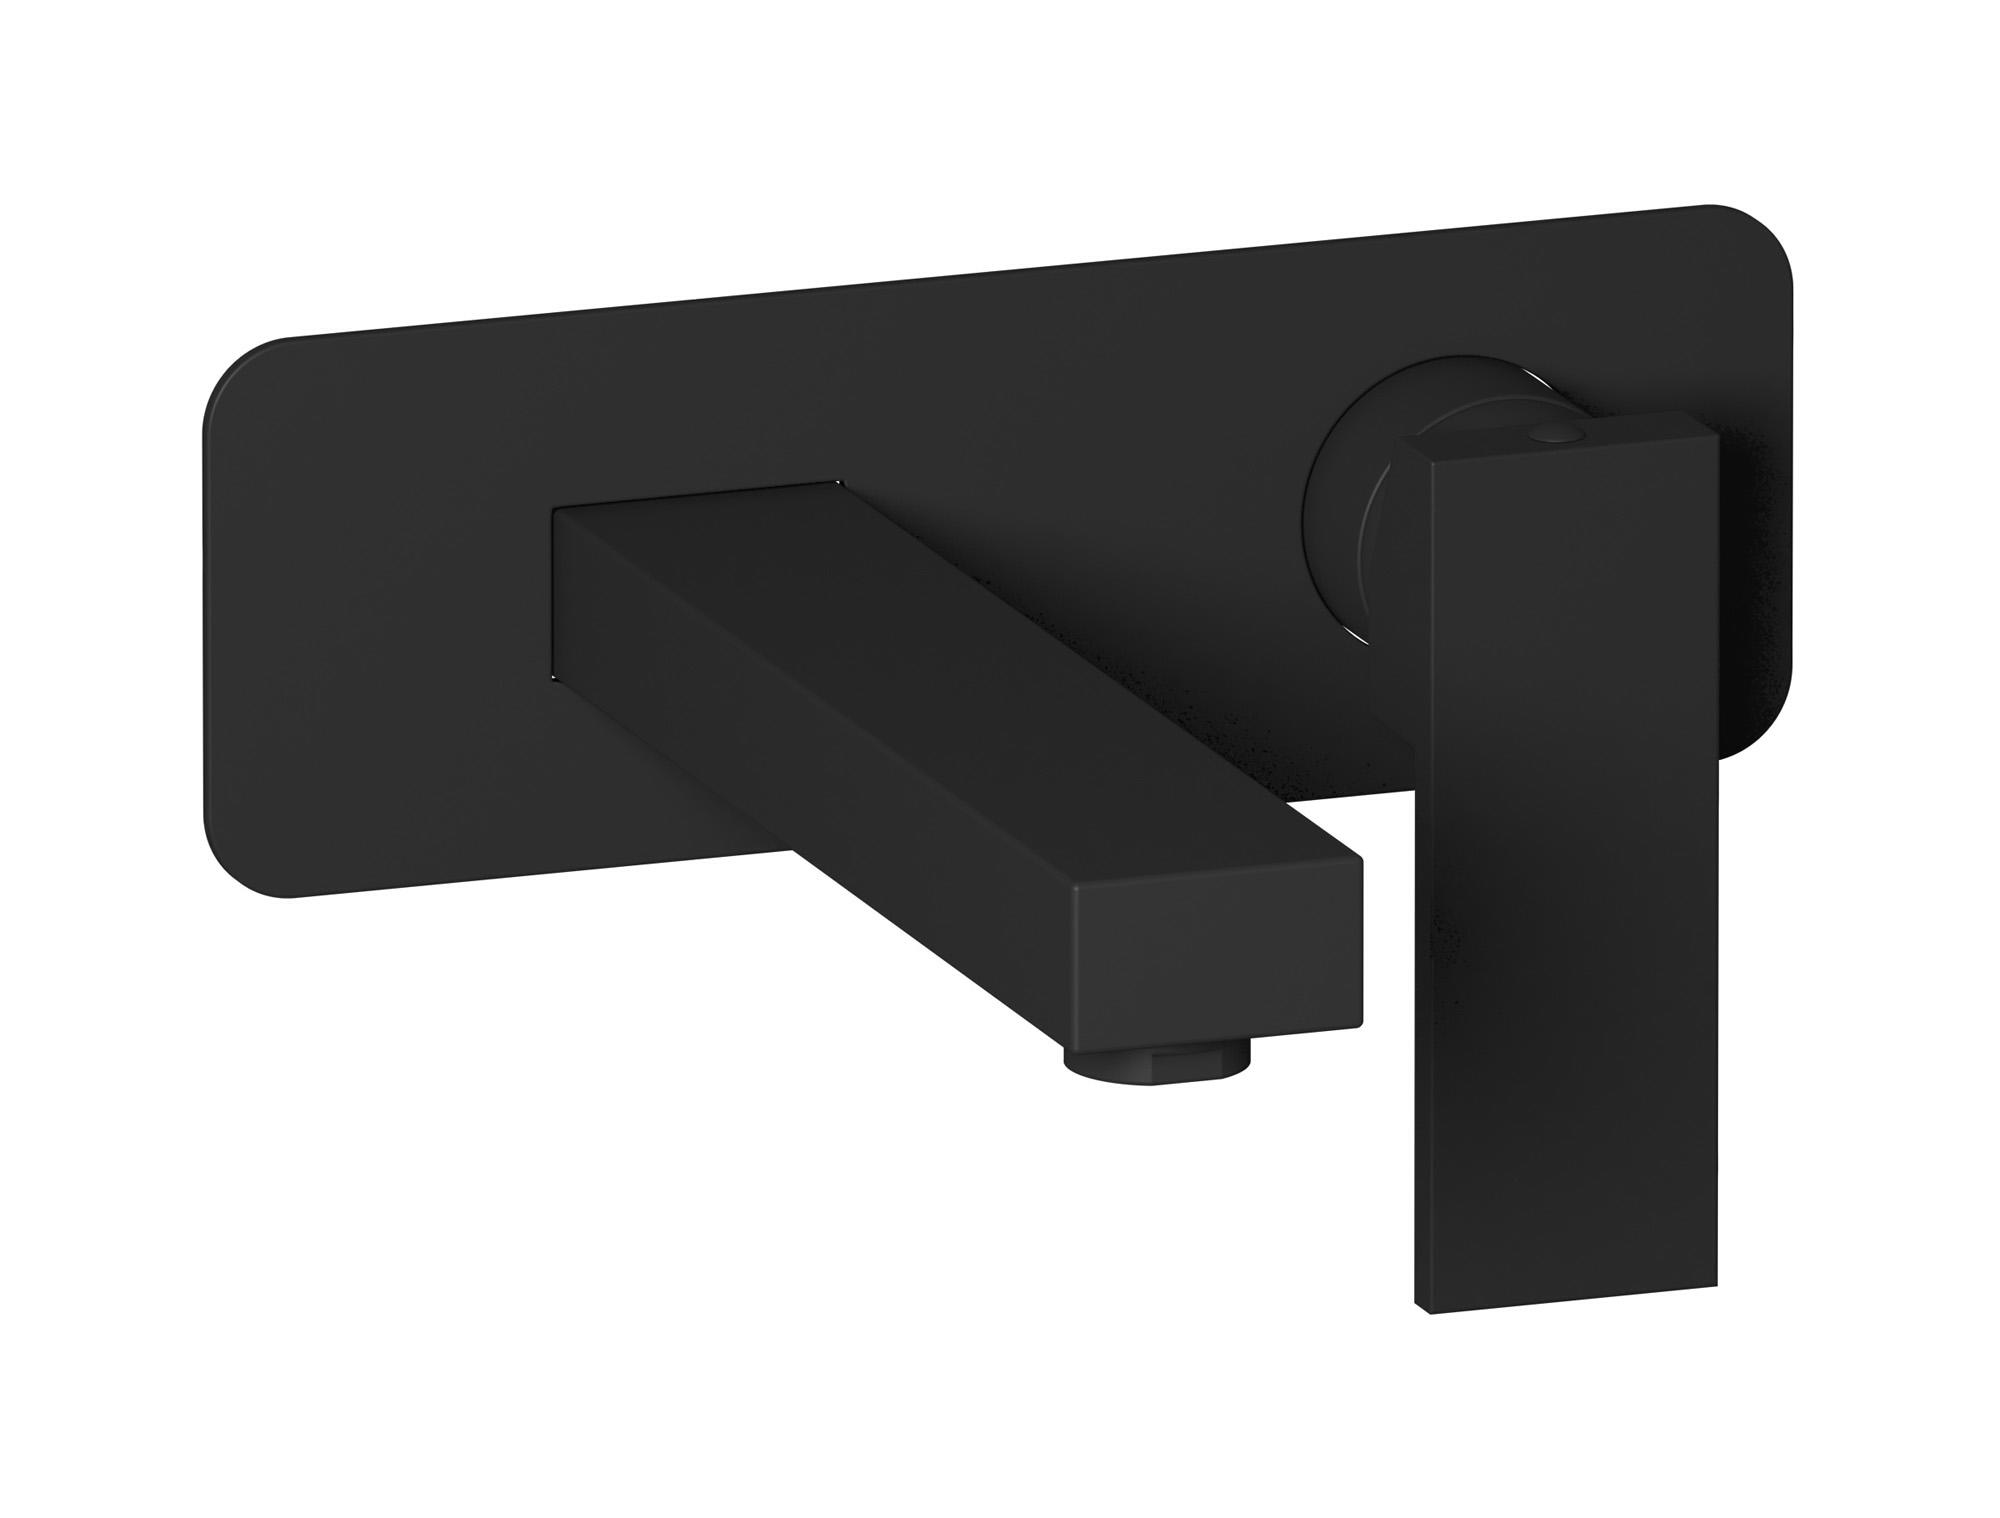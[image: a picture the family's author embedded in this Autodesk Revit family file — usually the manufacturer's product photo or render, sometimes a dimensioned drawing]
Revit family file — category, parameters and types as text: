
# Revit family: RU206
name_source: partatom
category: Apparecchi idraulici
units: mm (PartAtom-declared; Revit-internal decimal feet)

## family parameters
Basato su piano di lavoro = No
Condiviso = No
Mantieni orientamento annotazione = No
Numero OmniClass = 23.45.55.17
Punto di calcolo locali = No
Quota connettore circolare = Usa diametro
Sempre verticale = Sì
Taglio con vuoti quando caricato = No
Tipo di parte = Normale
Titolo OmniClass = Mixing Faucets

## types (12) — shared parameters
Cold water inlet = 10 mm  [stored 0.0328084 ft]
Commenti sul tipo = Wall mounted washbasin mixer complete with drain
Connessione CW = No
Connessione HW = No
Connessione di scarico = No
Connessione di ventilazione = No
Descrizione = Wall mounted washbasin mixer complete with drain
Hot water inlet = 10 mm  [stored 0.0328084 ft]
Produttore = IB Rubinetterie S.p.A.
URL = https://www.weareib.it
zero-valued in all types: Prospetto di default

## per-type parameters (varying)
| type | Finishes surface | Immagine tipo | Modello |
| Matt White | IB_matt white | RU206BO.jpg | RU206BO |
| Chrome | IB_Chrome | RU206CC.jpg | RU206CC |
| Black Chrome | IB_Black chrome | RU206CF.jpg | RU206CF |
| Brushed Black Chrome | IB_Brushed black chrome | RU206CS.jpg | RU206CS |
| Pale Gold | IB_Pale gold | RU206II.jpg | RU206II |
| Brushed Pale Gold | IB_brushed pale gold | RU206IS.jpg | RU206IS |
| Matt Black | IB_matt black | RU206NP.jpg | RU206NP |
| Gold | IB_gold | RU206OO.jpg | RU206OO |
| Brushed Gold | IB_brushed gold | RU206OS.jpg | RU206OS |
| Rose Gold | IB_Rose gold | RU206RS.jpg | RU206RS |
| Brushed Rose Gold | IB_Brushed rose gold | RU206SR.jpg | RU206SR |
| Brushed Nickel | IB_Brushed nickel | RU206SS.jpg | RU206SS |

note: [stored X ft] marks values corroborated as IEEE doubles in the binary element streams (Revit-internal decimal feet)
